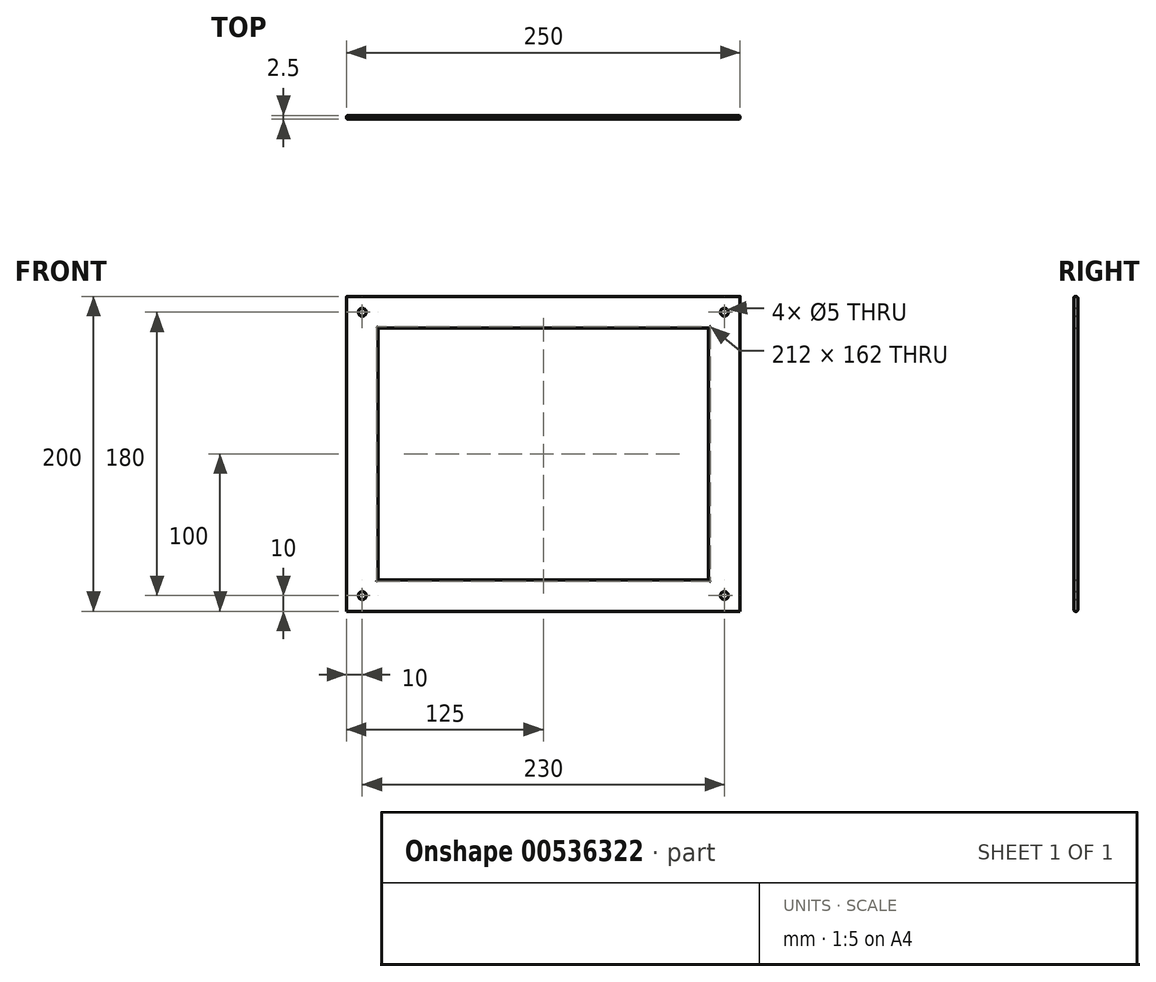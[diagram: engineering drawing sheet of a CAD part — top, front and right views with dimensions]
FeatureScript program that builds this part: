
annotation { "Feature Type Name" : "Feature", "Feature Type Description" : "" }
export const myFeature = defineFeature(function(context is Context, id is Id, definition is map)
    precondition{}
    {
        {
            var Q0;
            Q0=qCreatedBy(makeId("Front.planeOp"),FACE);
            var sketch = newSketch(context, id + "F0", { "sketchPlane" : qUnion([Q0])});
            skLineSegment(sketch, "E0.bottom", {"start": v(-125, 100) * mm, "end": v(125, 100) * mm});
            skLineSegment(sketch, "E0.top", {"start": v(-125, -100) * mm, "end": v(125, -100) * mm});
            skLineSegment(sketch, "E0.left", {"start": v(-125, 100) * mm, "end": v(-125, -100) * mm});
            skLineSegment(sketch, "E0.right", {"start": v(125, 100) * mm, "end": v(125, -100) * mm});
            skPoint(sketch, "E0.middle", {"position": v(0, 0) * mm});
            skLineSegment(sketch, "E1.bottom", {"start": v(-105, 80) * mm, "end": v(105, 80) * mm});
            skLineSegment(sketch, "E1.top", {"start": v(-105, -80) * mm, "end": v(105, -80) * mm});
            skLineSegment(sketch, "E1.left", {"start": v(-105, 80) * mm, "end": v(-105, -80) * mm});
            skLineSegment(sketch, "E1.right", {"start": v(105, 80) * mm, "end": v(105, -80) * mm});
            skCircle(sketch, "E2", {"center": v(-115, 90) * mm, "radius": 2.5 * mm});
            skCircle(sketch, "E3", {"center": v(-115, -90) * mm, "radius": 2.5 * mm});
            skCircle(sketch, "E4", {"center": v(115, -90) * mm, "radius": 2.5 * mm});
            skCircle(sketch, "E5", {"center": v(115, 90) * mm, "radius": 2.5 * mm});
            skLineSegment(sketch, "E6", {"start": v(-113.23, 88.23) * mm, "end": v(-116.77, 91.77) * mm});
            skLineSegment(sketch, "E7", {"start": v(-113.23, -88.23) * mm, "end": v(-116.77, -91.77) * mm});
            skLineSegment(sketch, "E8", {"start": v(113.23, -88.23) * mm, "end": v(116.77, -91.77) * mm});
            skLineSegment(sketch, "E9", {"start": v(113.23, 88.23) * mm, "end": v(116.77, 91.77) * mm});
            skSolve(sketch);
        }
        {
            var Q0;
            Q0=makeQuery(id+"F0.imprint","IMPRINT",FACE,{"disambiguationData":[TD([[makeQuery(id+"F0.imprint","IMPRINT",EDGE,{"derivedFrom":sQuery(id+"F0.wireOp",EDGE,"E0.bottom")}),-1.0]])]});
            extrude(context, id + "F1", {"entities" : qUnion([Q0]), "endBound" : BoundingType.SYMMETRIC, "depth" : 2.5 * mm, "offsetDistance" : 25 * mm});
        }
        {
            var Q0;
            Q0=makeQuery(id+"F1.opExtrude","CAP_EDGE",EDGE,{"disambiguationData":[OSD([sQuery(id+"F0.wireOp",EDGE,"E0.top")])],"isStart":true});
            var Q1;
            Q1=makeQuery(id+"F1.opExtrude","CAP_EDGE",EDGE,{"disambiguationData":[OSD([sQuery(id+"F0.wireOp",EDGE,"E0.top")])],"isStart":false});
            var Q2;
            Q2=makeQuery(id+"F1.opExtrude","CAP_EDGE",EDGE,{"disambiguationData":[OSD([sQuery(id+"F0.wireOp",EDGE,"E0.left")])],"isStart":false});
            var Q3;
            Q3=makeQuery(id+"F1.opExtrude","CAP_EDGE",EDGE,{"disambiguationData":[OSD([sQuery(id+"F0.wireOp",EDGE,"E0.left")])],"isStart":true});
            var Q4;
            Q4=makeQuery(id+"F1.opExtrude","CAP_EDGE",EDGE,{"disambiguationData":[OSD([sQuery(id+"F0.wireOp",EDGE,"E0.bottom")])],"isStart":true});
            var Q5;
            Q5=makeQuery(id+"F1.opExtrude","CAP_EDGE",EDGE,{"disambiguationData":[OSD([sQuery(id+"F0.wireOp",EDGE,"E0.bottom")])],"isStart":false});
            var Q6;
            Q6=makeQuery(id+"F1.opExtrude","CAP_EDGE",EDGE,{"disambiguationData":[OSD([sQuery(id+"F0.wireOp",EDGE,"E0.right")])],"isStart":false});
            var Q7;
            Q7=makeQuery(id+"F1.opExtrude","CAP_EDGE",EDGE,{"disambiguationData":[OSD([sQuery(id+"F0.wireOp",EDGE,"E0.right")])],"isStart":true});
            var Q8;
            Q8=makeQuery(id+"F1.opExtrude","CAP_EDGE",EDGE,{"disambiguationData":[OSD([sQuery(id+"F0.wireOp",EDGE,"E1.top")])],"isStart":false});
            var Q9;
            Q9=makeQuery(id+"F1.opExtrude","CAP_EDGE",EDGE,{"disambiguationData":[OSD([sQuery(id+"F0.wireOp",EDGE,"E1.top")])],"isStart":true});
            var Q10;
            Q10=makeQuery(id+"F1.opExtrude","CAP_EDGE",EDGE,{"disambiguationData":[OSD([sQuery(id+"F0.wireOp",EDGE,"E1.left")])],"isStart":true});
            var Q11;
            Q11=makeQuery(id+"F1.opExtrude","CAP_EDGE",EDGE,{"disambiguationData":[OSD([sQuery(id+"F0.wireOp",EDGE,"E1.left")])],"isStart":false});
            var Q12;
            Q12=makeQuery(id+"F1.opExtrude","CAP_EDGE",EDGE,{"disambiguationData":[OSD([sQuery(id+"F0.wireOp",EDGE,"E1.bottom")])],"isStart":false});
            var Q13;
            Q13=makeQuery(id+"F1.opExtrude","CAP_EDGE",EDGE,{"disambiguationData":[OSD([sQuery(id+"F0.wireOp",EDGE,"E1.bottom")])],"isStart":true});
            var Q14;
            Q14=makeQuery(id+"F1.opExtrude","CAP_EDGE",EDGE,{"disambiguationData":[OSD([sQuery(id+"F0.wireOp",EDGE,"E1.right")])],"isStart":true});
            var Q15;
            Q15=makeQuery(id+"F1.opExtrude","CAP_EDGE",EDGE,{"disambiguationData":[OSD([sQuery(id+"F0.wireOp",EDGE,"E1.right")])],"isStart":false});
            fillet(context, id + "F2", {"entities" : qUnion([Q0, Q1, Q2, Q3, Q4, Q5, Q6, Q7, Q8, Q9, Q10, Q11, Q12, Q13, Q14, Q15]), "radius" : 1 * mm, "tangentPropagation" : true, "allowEdgeOverflow" : false});
        }
    });
